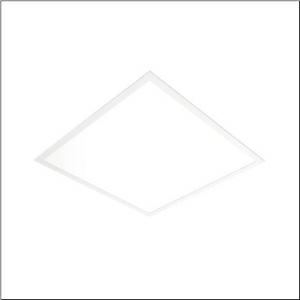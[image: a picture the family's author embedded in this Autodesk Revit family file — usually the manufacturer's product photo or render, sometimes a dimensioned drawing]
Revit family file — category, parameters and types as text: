
# Revit family: apollon_r__41_51mh11w72322_d4b8
name_source: partatom
category: Lighting Fixtures
units: mm (PartAtom-declared; Revit-internal decimal feet)

## family parameters
Cut with Voids When Loaded = No
Host = Face
Light Source = No
Part Type = Normal
Room Calculation Point = No
Round Connector Dimension = Use Diameter
Shared = No

## types (1)
- Apollon® 41 (1 x LED, 3550 lm, 35 W, 3000K)
    Apparent Load = 35 VA
    CIE Flux Codes = 63 87 97 100 100
    Color Rendering = 80
    Color Temperature = 3000K
    Default Elevation = 1800 mm
    Description = Apollon® 41, office luminaire, primary optical cover: prismatic diffuser, of PS, light emission: direct distribution, primary light characteristic: symmetric, installation type: lay-in mounting, LED rated luminous flux: 3.550 lm, light colour: 830, colour temperature: 3000K, control gear: ECG, with terminal, 3-pole, mains connection: 220..240V, AC, 50/60Hz, rated input power: 35W, housing, of aluminium section, traffic white (RAL 9016), module: M625, length: 622 mm, width: 622 mm, height: 30mm, housing upper side, of sheet steel, protection rating (complete): IP20, protection rating (lamp compartment, on room side): IP40, insulation class (complete): insulation class II (safety insulation), certification: CE, ENEC, permissible ambient temperature for indoor applications: -20..+40°C, packaging unit: 1 piece
    Height = 0 mm  [stored 0 ft]
    Lamp = 1 x LED
    Lamp Light Flux = 3550 lm
    Lamp Power = 35 W
    Lamp count = 1
    Length = 620 mm
    Luminous efficacy = 101 lm/W
    Manufacturer = Siteco
    ModVariant = No
    Model = 51MH11W72322
    Mounting Place = Ceiling
    Mounting Type = Recessed
    Number of Poles = 1
    OnlyDefault = Yes
    Power Factor = 1
    Product Name = Apollon® 41
    Product group = office luminaire | ceiling recessed
    ProductGroupID = 400
    Protection Class = Protection class II
    Protection Degree = IP 20
    RLX_Detail_Level = 1
    RlxData = <blob elided: 14821 chars, md5=83188e8b>
    Socket = socket
    Standby Power = 0 W
    System Light Flux = 3550 lm
    System Power = 35 W
    Type Comments = Product without accessories
    Type Image = l_1003755.jpg
    URL = http://relux.com
    VarID = ---
    Voltage = 0 V
    Weight = 0.00 kg
    Width = 620 mm

note: [stored X ft] marks values corroborated as IEEE doubles in the binary element streams (Revit-internal decimal feet)

## geometry (parser evidence)
native form markers: Sweep x11
no freeform markers — native parametric forms only
